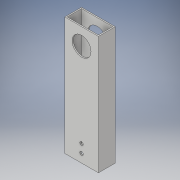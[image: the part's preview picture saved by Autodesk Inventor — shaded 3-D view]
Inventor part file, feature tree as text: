
AUTODESK INVENTOR PART (.ipt)
format: ipt  version: 2018 (Build 220112000, 112)  size: 126,464 bytes
history: native  units: in
note: dims shown in document units (in); Inventor stores cm internally (conversion verified against a paired STEP export)
features: extrude x3, sketch x3
ambient origin geometry x8: Origin, YZ Plane, XZ Plane, XY Plane, X Axis, Y Axis, Z Axis, Center Point
bodies: Solid1 (feature_tree)
feature tree (6):
  extrude  "Extrusion1"  Depth=7.0in
  extrude  "Extrusion2"  Depth=0.075in
  extrude  "Extrusion3"  Depth=1.0in
  sketch  "Sketch1"  dims[d0=2.0in d1=7.0in]
  sketch  "Sketch2"  dims[d2=1.0in d3=0.0in d4=0.075in]
  sketch  "Sketch3"  dims[d5=20.0in d6=0.0in d7=0.5in d8=0.5in d9=1.0in d10=1.1225in d11=0.2031in d12=0.2031in d13=20.0in d14=0.0in]
